# Revit family: NBS_HeatraeSadia_WtrSplyFitngsForSnks_AquatapDispenser
name_source: partatom
category: Plumbing Fixtures
revit_build: Autodesk Revit 2014 (Build: 20130709_2115(x64)
units: mm (PartAtom-declared; Revit-internal decimal feet)

## types (3) — shared parameters
AssetType = Fixed
Default Elevation = 1200 mm
Depth = 118 mm
DispenserSafetyFeatures = Integral dual action safety feature to prevent accidental boiling water delivery, boiling water delivery indicator LED
DispenserSize = 235 x 60 x 118 mm (h x w x l)
DurationUnit = year
FaucetOperation = Other
FaucetTopDescription = Electronic buttons
FaucetType = Other
Features = Undercounter design, LED indicators, Intelliboil™Plus technology
Finish = Chrome plated body and buttons
HW Connection = Yes
HasProtectiveEarth = No
HeaterSafetyFeatures = Low pressure vented, dry start protection by self-resetting bi-metal thermal cut-out, boil-dry protection by manually-resettable bi-metal cut-out
HeaterSize = 480 x 350 x 296 mm (h x w x l)
HeaterWaterCapacity = 5 L
Height = 235 mm  [stored 0.770997 ft]
IPCode = IPX2
IfcExportAs = IfcValveType
IfcExportType = FAUCET
IntegralAccessories = Drip tray, Extension piece, Programmable timer, Water filter cartridge, Water filter system
ManufacturerName = Heatrae Sadia
ManufacturerURL = www.heatraesadia.com
NBSCertification = http://www.nationalbimlibrary.com
NBSDescription = Water supply fittings for sinks
NBSNote = 90-15-35/440
NBSReference = 45-35-70/345
NominalFrequencyRange = 0
NominalHeight = 235 mm  [stored 0.770997 ft]
NominalLength = 118 mm
NominalVoltage = 230.0, 240.0
NominalWidth = 60 mm  [stored 0.19685 ft]
PhaseAngle = 0.00°
ProductInformation = www.heatraesadia.com/docs/Drinking_water_brochure.pdf
Uniclass2 = 45-45-47/479
Uniclass2015Description = Sink manual water supply sets
Uniclass2015Reference = Pr_40_20_87_82
Uniclass2015Version = Products v1.1
Vent Connection = Yes
Version = 1
WarrantyDurationLabor = 2
WarrantyDurationParts = 2
WarrantyDurationUnit = year
WarrantyStartDate = 1900-12-31T23:59:59
Waste Connection = No
WaterOutletHeight = 181 mm
WaterSupplyTemperatureMaximum = 100°C
Width = 60 mm  [stored 0.19685 ft]
zero-valued in all types: ElectricalDeviceNominalPower, NominalCurrent, NumberOfPoles, UsageCurrent

## per-type parameters (varying)
| type | BIMObjectName | CW Connection | ChilledWaterOutput | ChillerSize | Color | Connections | Description | FaucetFunction | Form | Material | ModelNumber | ModelReference | Name | SupplyPressureRange | Thermostat |
| Boiling | NBS_HeatraeSadia_WaterSupplyFittingsForSinks_AquatapDispenser_Boiling | No |  |  | Dispenser: Chrome; Water heater: White | Two 0.5 m hoses | Boiling water dispenser and heater | Boiling | Boiling water dispenser with undercounter water heater | Dispenser: Die cast metal; Water heater casing: High impact thermoplastic; Water container: Moulded polyphenylene sulphide | 95:200:261 | Aquatap Boiling | WaterSupplyFittingsForSinks_AquatapDispenser_Boiling_HeatraeSadia | 0.5-10.0 bar | Electronic to control water temperature up to boiling point |
| Boiling/Ambient | NBS_HeatraeSadia_WaterSupplyFittingsForSinks_AquatapDispenser_Boiling/Ambient | Yes |  |  | Dispenser: Chrome; Water heater: White | Three 0.5 m hoses | Boiling/ambient water dispenser and heater | Boiling and ambient | Boiling and ambient water dispenser with undercounter water heater | Dispenser: Die cast metal; Water heater casing: High impact thermoplastic; Water container: Moulded polyphenylene sulphide | 95:200:263 | Aquatap Boiling/Ambient | WaterSupplyFittingsForSinks_AquatapDispenser_Boiling/Ambient_HeatraeSadia | 0.5-10.0 bar | Electronic to control water temperature up to boiling point |
| Boiling/Chilled | NBS_HeatraeSadia_WaterSupplyFittingsForSinks_AquatapDispenser_Boiling/Chilled | Yes | 30 L/hour (at 10ºC). | 405 x 255 x 400 mm (h x w x l) | Dispenser: Chrome; Water heater: White; Chiller: Brushed | Three 0.5 m hoses | Boiling/chilled water dispenser and heater | Boiling and chilled | Boiling and chilled water dispenser with undercounter water heater | Dispenser: Die cast metal; Water heater casing: High impact thermoplastic; Water container: Moulded polyphenylene sulphide; Chiller casing: Stainless steel effect plastic coated corrosion-proofed steel | 95:200:262 | Aquatap Boiling/Chilled | WaterSupplyFittingsForSinks_AquatapDispenser_Boiling/Chilled_HeatraeSadia | Heater: 0.5-10.0 bar; Chiller: 1.0-3.0 bar | Heater: Electronic to control water temperature up to boiling point; Chiller: Adjustable from 3–10ºC. |

note: [stored X ft] marks values corroborated as IEEE doubles in the binary element streams (Revit-internal decimal feet)

## geometry (parser evidence)
native form markers: Sweep x3
no freeform markers — native parametric forms only
